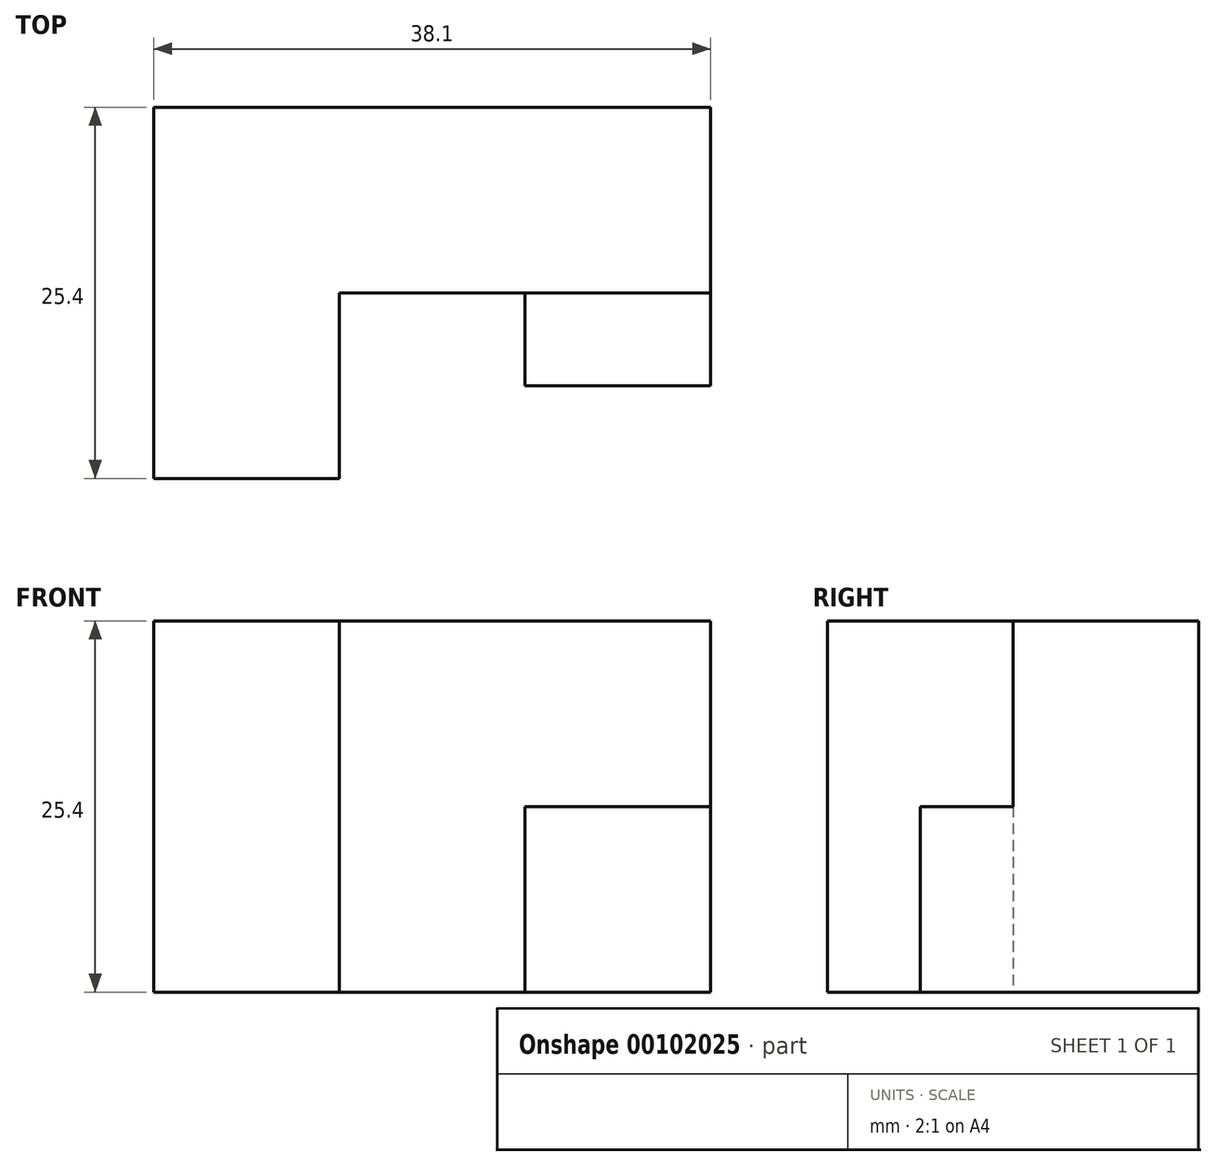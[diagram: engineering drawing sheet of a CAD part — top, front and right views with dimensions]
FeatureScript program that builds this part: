
annotation { "Feature Type Name" : "Feature", "Feature Type Description" : "" }
export const myFeature = defineFeature(function(context is Context, id is Id, definition is map)
    precondition{}
    {
        {
            var Q0;
            Q0=qCreatedBy(makeId("Top.planeOp"),FACE);
            var sketch = newSketch(context, id + "F0", { "sketchPlane" : qUnion([Q0])});
            skLineSegment(sketch, "E0", {"start": v(0, 0) * mm, "end": v(0, 25.4) * mm});
            skLineSegment(sketch, "E1", {"start": v(0, 25.4) * mm, "end": v(38.1, 25.4) * mm});
            skLineSegment(sketch, "E2", {"start": v(38.1, 25.4) * mm, "end": v(38.1, 12.7) * mm});
            skLineSegment(sketch, "E3", {"start": v(38.1, 12.7) * mm, "end": v(12.7, 12.7) * mm});
            skLineSegment(sketch, "E4", {"start": v(12.7, 12.7) * mm, "end": v(12.7, 0) * mm});
            skLineSegment(sketch, "E5", {"start": v(12.7, 0) * mm, "end": v(0, 0) * mm});
            skLineSegment(sketch, "E6", {"start": v(38.1, 12.7) * mm, "end": v(38.1, 6.35) * mm});
            skLineSegment(sketch, "E7", {"start": v(38.1, 6.35) * mm, "end": v(25.4, 6.35) * mm});
            skLineSegment(sketch, "E8", {"start": v(25.4, 6.35) * mm, "end": v(25.4, 12.7) * mm});
            skSolve(sketch);
        }
        {
            var Q0;
            Q0=makeQuery(id+"F0.imprint","IMPRINT",FACE,{"disambiguationData":[TD([[makeQuery(id+"F0.imprint","IMPRINT",EDGE,{"derivedFrom":sQuery(id+"F0.wireOp",EDGE,"E0")}),-1.0]])]});
            extrude(context, id + "F1", {"entities" : qUnion([Q0]), "depth" : 25.4 * mm});
        }
        {
            var Q0;
            Q0 = qSketchRegion(id + "F0", true);
            extrude(context, id + "F2", {"entities" : qUnion([Q0]), "operationType" : NewBodyOperationType.ADD, "depth" : 12.7 * mm});
        }
    });
